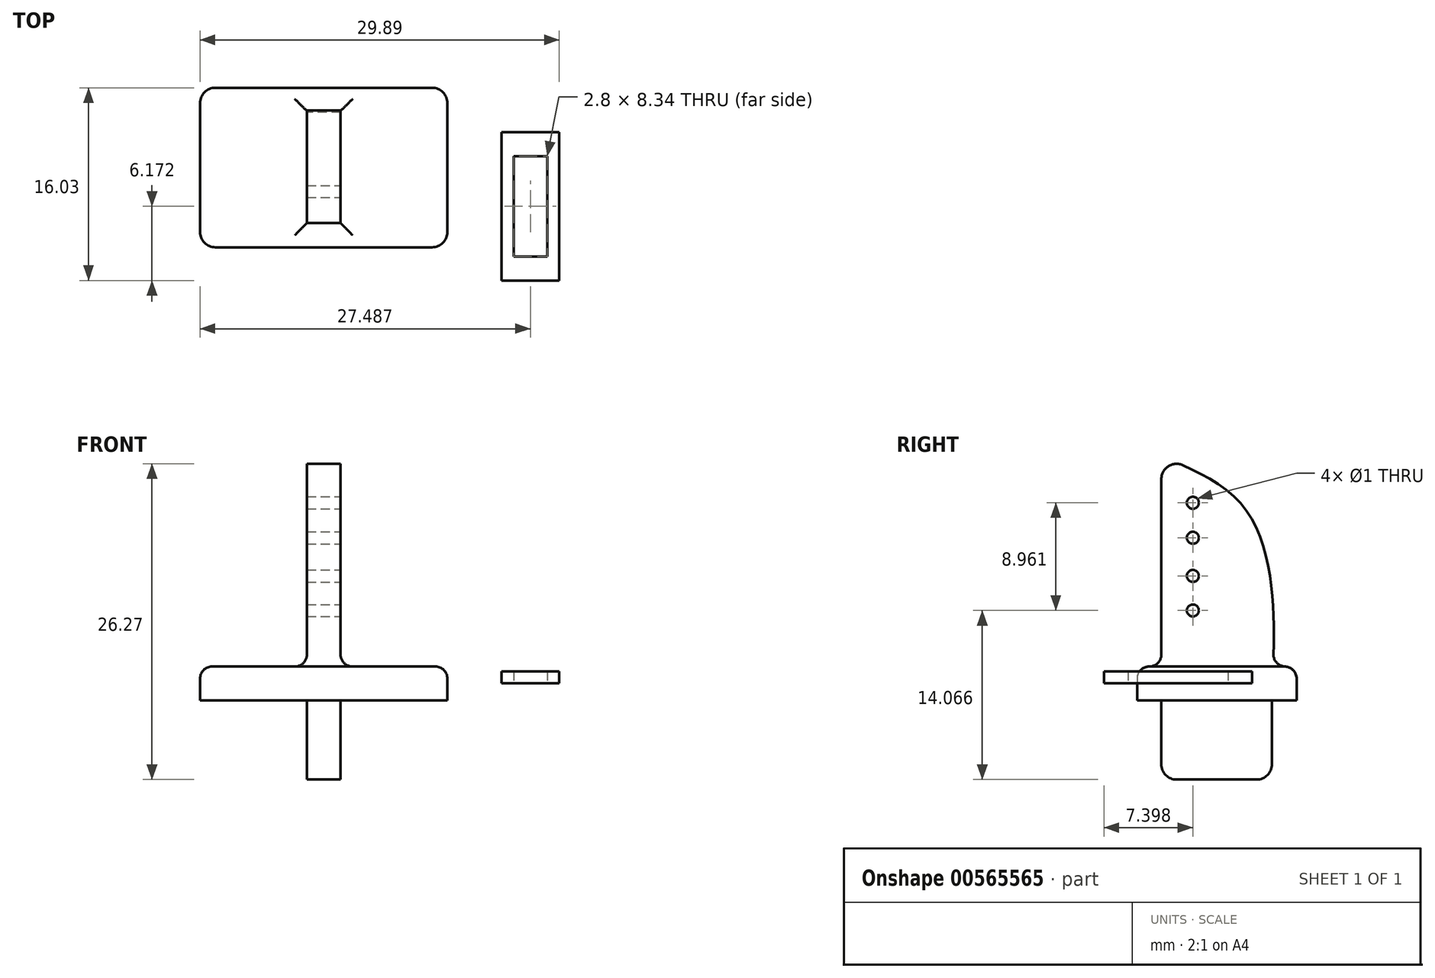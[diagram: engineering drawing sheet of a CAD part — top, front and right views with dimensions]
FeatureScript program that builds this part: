
annotation { "Feature Type Name" : "Feature", "Feature Type Description" : "" }
export const myFeature = defineFeature(function(context is Context, id is Id, definition is map)
    precondition{}
    {
        {
            var Q0;
            Q0=qCreatedBy(makeId("Top.planeOp"),FACE);
            var sketch = newSketch(context, id + "F0", { "sketchPlane" : qUnion([Q0])});
            skLineSegment(sketch, "E0.bottom", {"start": v(10.29, -6.63) * mm, "end": v(-10.29, -6.63) * mm});
            skLineSegment(sketch, "E0.top", {"start": v(10.29, 6.63) * mm, "end": v(-10.29, 6.63) * mm});
            skLineSegment(sketch, "E0.left", {"start": v(10.29, -6.63) * mm, "end": v(10.29, 6.63) * mm});
            skLineSegment(sketch, "E0.right", {"start": v(-10.29, -6.63) * mm, "end": v(-10.29, 6.63) * mm});
            skPoint(sketch, "E0.middle", {"position": v(0, 0) * mm});
            skLineSegment(sketch, "E1", {"start": v(0, 6.63) * mm, "end": v(0, -6.63) * mm});
            skPoint(sketch, "E2", {"position": v(0, 4.47) * mm});
            skPoint(sketch, "E3", {"position": v(0, -3.66) * mm});
            skSolve(sketch);
        }
        {
            var Q0;
            Q0=qCreatedBy(makeId("Right.planeOp"),FACE);
            var sketch = newSketch(context, id + "F1", { "sketchPlane" : qUnion([Q0])});
            skLineSegment(sketch, "E4", {"start": v(-4.62, 0) * mm, "end": v(-4.62, 19) * mm});
            skLineSegment(sketch, "E5", {"start": v(-4.62, 0) * mm, "end": v(-4.62, -8) * mm});
            skLineSegment(sketch, "E6", {"start": v(-4.62, -8) * mm, "end": v(4.58, -8) * mm});
            skLineSegment(sketch, "E7", {"start": v(4.58, 0) * mm, "end": v(4.58, -8) * mm});
            skFitSpline(sketch, "E8", {"points": [v(4.58, 0) * mm, v(4.58, 7.59) * mm, v(1.93, 15.03) * mm, v(-4.62, 19) * mm], "startDerivative": vector(1.47, 21.84) * mm, "endDerivative": vector(-18.58, 9.08) * mm});
            skPoint(sketch, "E9", {"position": v(-2, 15.03) * mm});
            skPoint(sketch, "E10", {"position": v(-2, 12.12) * mm});
            skPoint(sketch, "E11", {"position": v(-2, 8.94) * mm});
            skPoint(sketch, "E12", {"position": v(-2, 6.07) * mm});
            skLineSegment(sketch, "E13", {"start": v(-2, -5.7) * mm, "end": v(-2, 21.25) * mm, "construction": true});
            skSolve(sketch);
        }
        {
            var Q0;
            Q0=makeQuery(id+"F1.imprint","IMPRINT",FACE,{"disambiguationData":[TD([[makeQuery(id+"F1.imprint","IMPRINT",EDGE,{"derivedFrom":sQuery(id+"F1.wireOp",EDGE,"E4")}),-1.0]])]});
            extrude(context, id + "F2", {"entities" : qUnion([Q0]), "endBound" : BoundingType.SYMMETRIC, "depth" : 2.8 * mm, "offsetDistance" : 25.4 * mm});
        }
        {
            var Q0;
            {var subQ0=sQuery(id+"F0.wireOp",EDGE,"E0.left");Q0=makeQuery(id+"F0.imprint","IMPRINT",FACE,{"disambiguationData":[TD([[makeQuery(id+"F0.imprint","IMPRINT",EDGE,{"derivedFrom":subQ0}),1.0]])]});}
            var Q1;
            {var subQ0=sQuery(id+"F0.wireOp",EDGE,"E0.right");Q1=makeQuery(id+"F0.imprint","IMPRINT",FACE,{"disambiguationData":[TD([[makeQuery(id+"F0.imprint","IMPRINT",EDGE,{"derivedFrom":subQ0}),-1.0]])]});}
            extrude(context, id + "F3", {"entities" : qUnion([Q0, Q1]), "operationType" : NewBodyOperationType.ADD, "endBound" : BoundingType.SYMMETRIC, "depth" : 2.8 * mm, "offsetDistance" : 25.4 * mm});
        }
        {
            var Q0;
            Q0=makeQuery(id+"F2.opExtrude","SWEPT_EDGE",EDGE,{"disambiguationData":[OSD([sQuery(id+"F1.wireOp",EDGE,"E5"),sQuery(id+"F1.wireOp",EDGE,"E6")])]});
            var Q1;
            Q1=makeQuery(id+"F2.opExtrude","SWEPT_EDGE",EDGE,{"disambiguationData":[OSD([sQuery(id+"F1.wireOp",EDGE,"E6"),sQuery(id+"F1.wireOp",EDGE,"E7")])]});
            var Q2;
            Q2=makeQuery(id+"F2.opExtrude","SWEPT_EDGE",EDGE,{"disambiguationData":[OSD([sQuery(id+"F1.wireOp",EDGE,"E4"),sQuery(id+"F1.wireOp",EDGE,"E8")])]});
            fillet(context, id + "F4", {"entities" : qUnion([Q0, Q1, Q2]), "radius" : 1.27 * mm, "tangentPropagation" : true, "allowEdgeOverflow" : false});
        }
        {
            var Q0;
            Q0=makeQuery(id+"F3.opExtrude","SWEPT_EDGE",EDGE,{"disambiguationData":[OSD([sQuery(id+"F0.wireOp",EDGE,"E0.bottom"),sQuery(id+"F0.wireOp",EDGE,"E0.left")])]});
            var Q1;
            Q1=makeQuery(id+"F3.opExtrude","SWEPT_EDGE",EDGE,{"disambiguationData":[OSD([sQuery(id+"F0.wireOp",EDGE,"E0.bottom"),sQuery(id+"F0.wireOp",EDGE,"E0.right")])]});
            var Q2;
            Q2=makeQuery(id+"F3.opExtrude","SWEPT_EDGE",EDGE,{"disambiguationData":[OSD([sQuery(id+"F0.wireOp",EDGE,"E0.top"),sQuery(id+"F0.wireOp",EDGE,"E0.right")])]});
            var Q3;
            Q3=makeQuery(id+"F3.opExtrude","SWEPT_EDGE",EDGE,{"disambiguationData":[OSD([sQuery(id+"F0.wireOp",EDGE,"E0.top"),sQuery(id+"F0.wireOp",EDGE,"E0.left")])]});
            fillet(context, id + "F5", {"entities" : qUnion([Q0, Q1, Q2, Q3]), "radius" : 1.27 * mm, "tangentPropagation" : true, "allowEdgeOverflow" : false});
        }
        {
            var Q0;
            Q0=makeQuery(id+"F3.opExtrude","CAP_EDGE",EDGE,{"disambiguationData":[OSD([sQuery(id+"F0.wireOp",EDGE,"E0.top")])],"isStart":false});
            fillet(context, id + "F6", {"entities" : qUnion([Q0]), "radius" : 1 * mm, "tangentPropagation" : true, "allowEdgeOverflow" : false});
        }
        {
            var Q0;
            Q0=makeQuery(id+"F3.boolean.opBoolean","INTERSECT",EDGE,{"derivedFrom":[makeQuery(id+"F2.opExtrude","CAP_FACE",FACE,{"disambiguationData":[OSD([sQuery(id+"F1.wireOp",EDGE,"E4"),sQuery(id+"F1.wireOp",EDGE,"E5"),sQuery(id+"F1.wireOp",EDGE,"E6"),sQuery(id+"F1.wireOp",EDGE,"E7"),sQuery(id+"F1.wireOp",EDGE,"E8")])],"isStart":false}),makeQuery(id+"F3.opExtrude","CAP_FACE",FACE,{"disambiguationData":[OSD([sQuery(id+"F0.wireOp",EDGE,"E0.bottom"),sQuery(id+"F0.wireOp",EDGE,"E0.top"),sQuery(id+"F0.wireOp",EDGE,"E0.left"),sQuery(id+"F0.wireOp",EDGE,"E0.right")])],"isStart":false})]});
            var Q1;
            Q1=makeQuery(id+"F3.boolean.opBoolean","INTERSECT",EDGE,{"derivedFrom":[makeQuery(id+"F2.opExtrude","SWEPT_FACE",FACE,{"disambiguationData":[OSD([sQuery(id+"F1.wireOp",EDGE,"E4"),sQuery(id+"F1.wireOp",EDGE,"E5")])]}),makeQuery(id+"F3.opExtrude","CAP_FACE",FACE,{"disambiguationData":[OSD([sQuery(id+"F0.wireOp",EDGE,"E0.bottom"),sQuery(id+"F0.wireOp",EDGE,"E0.top"),sQuery(id+"F0.wireOp",EDGE,"E0.left"),sQuery(id+"F0.wireOp",EDGE,"E0.right")])],"isStart":false})]});
            var Q2;
            Q2=makeQuery(id+"F3.boolean.opBoolean","INTERSECT",EDGE,{"derivedFrom":[makeQuery(id+"F2.opExtrude","CAP_FACE",FACE,{"disambiguationData":[OSD([sQuery(id+"F1.wireOp",EDGE,"E4"),sQuery(id+"F1.wireOp",EDGE,"E5"),sQuery(id+"F1.wireOp",EDGE,"E6"),sQuery(id+"F1.wireOp",EDGE,"E7"),sQuery(id+"F1.wireOp",EDGE,"E8")])],"isStart":true}),makeQuery(id+"F3.opExtrude","CAP_FACE",FACE,{"disambiguationData":[OSD([sQuery(id+"F0.wireOp",EDGE,"E0.bottom"),sQuery(id+"F0.wireOp",EDGE,"E0.top"),sQuery(id+"F0.wireOp",EDGE,"E0.left"),sQuery(id+"F0.wireOp",EDGE,"E0.right")])],"isStart":false})]});
            var Q3;
            Q3=makeQuery(id+"F3.boolean.opBoolean","INTERSECT",EDGE,{"derivedFrom":[makeQuery(id+"F2.opExtrude","SWEPT_FACE",FACE,{"disambiguationData":[OSD([sQuery(id+"F1.wireOp",EDGE,"E8")])]}),makeQuery(id+"F3.opExtrude","CAP_FACE",FACE,{"disambiguationData":[OSD([sQuery(id+"F0.wireOp",EDGE,"E0.bottom"),sQuery(id+"F0.wireOp",EDGE,"E0.top"),sQuery(id+"F0.wireOp",EDGE,"E0.left"),sQuery(id+"F0.wireOp",EDGE,"E0.right")])],"isStart":false})]});
            fillet(context, id + "F7", {"entities" : qUnion([Q0, Q1, Q2, Q3]), "radius" : 1 * mm, "tangentPropagation" : true, "allowEdgeOverflow" : false});
        }
        {
            var Q0;
            Q0=sQuery(id+"F1.wireOp",VERTEX,"E9");
            var Q1;
            Q1=sQuery(id+"F1.wireOp",VERTEX,"E10");
            var Q2;
            Q2=sQuery(id+"F1.wireOp",VERTEX,"E11");
            var Q3;
            Q3=sQuery(id+"F1.wireOp",VERTEX,"E12");
            var Q4;
            Q4=makeQuery(id+"F2.opExtrude","SWEPT_BODY",BODY,{"disambiguationData":[OSD([sQuery(id+"F1.wireOp",EDGE,"E4"),sQuery(id+"F1.wireOp",EDGE,"E5"),sQuery(id+"F1.wireOp",EDGE,"E6"),sQuery(id+"F1.wireOp",EDGE,"E7"),sQuery(id+"F1.wireOp",EDGE,"E8")])]});
            hole(context, id + "F8", {"style" : HoleStyle.SIMPLE, "endStyle" : HoleEndStyle.THROUGH, "holeDiameter" : 1 * mm, "majorDiameter" : 5 * mm, "isTappedThrough" : true, "tappedDepth" : 12.7 * mm, "tapClearance" : 3, "startFromSketch" : true, "locations" : qUnion([Q0, Q1, Q2, Q3]), "scope" : qUnion([Q4])});
        }
        {
            var Q0;
            Q0=sQuery(id+"F1.wireOp",VERTEX,"E9");
            var Q1;
            Q1=sQuery(id+"F1.wireOp",VERTEX,"E10");
            var Q2;
            Q2=sQuery(id+"F1.wireOp",VERTEX,"E11");
            var Q3;
            Q3=sQuery(id+"F1.wireOp",VERTEX,"E12");
            var Q4;
            Q4=makeQuery(id+"F2.opExtrude","SWEPT_BODY",BODY,{"disambiguationData":[OSD([sQuery(id+"F1.wireOp",EDGE,"E4"),sQuery(id+"F1.wireOp",EDGE,"E5"),sQuery(id+"F1.wireOp",EDGE,"E6"),sQuery(id+"F1.wireOp",EDGE,"E7"),sQuery(id+"F1.wireOp",EDGE,"E8")])]});
            hole(context, id + "F9", {"style" : HoleStyle.SIMPLE, "endStyle" : HoleEndStyle.THROUGH, "oppositeDirection" : true, "holeDiameter" : 1 * mm, "majorDiameter" : 5 * mm, "isTappedThrough" : true, "tappedDepth" : 12.7 * mm, "tapClearance" : 3, "startFromSketch" : true, "locations" : qUnion([Q0, Q1, Q2, Q3]), "scope" : qUnion([Q4])});
        }
        {
            var Q0;
            Q0=qCreatedBy(makeId("Top.planeOp"),FACE);
            var sketch = newSketch(context, id + "F10", { "sketchPlane" : qUnion([Q0])});
            skLineSegment(sketch, "E14.bottom", {"start": v(18.6, -7.4) * mm, "end": v(15.8, -7.4) * mm});
            skLineSegment(sketch, "E14.top", {"start": v(18.6, 0.94) * mm, "end": v(15.8, 0.94) * mm});
            skLineSegment(sketch, "E14.left", {"start": v(18.6, -7.4) * mm, "end": v(18.6, 0.94) * mm});
            skLineSegment(sketch, "E14.right", {"start": v(15.8, -7.4) * mm, "end": v(15.8, 0.94) * mm});
            skLineSegment(sketch, "E15.bottom", {"start": v(19.6, -9.4) * mm, "end": v(14.8, -9.4) * mm});
            skLineSegment(sketch, "E15.top", {"start": v(19.6, 2.94) * mm, "end": v(14.8, 2.94) * mm});
            skLineSegment(sketch, "E15.left", {"start": v(19.6, -9.4) * mm, "end": v(19.6, 2.94) * mm});
            skLineSegment(sketch, "E15.right", {"start": v(14.8, -9.4) * mm, "end": v(14.8, 2.94) * mm});
            skSolve(sketch);
        }
        {
            var Q0;
            Q0=makeQuery(id+"F10.imprint","IMPRINT",FACE,{"disambiguationData":[TD([[makeQuery(id+"F10.imprint","IMPRINT",EDGE,{"derivedFrom":sQuery(id+"F10.wireOp",EDGE,"E14.bottom")}),1.0]])]});
            extrude(context, id + "F11", {"entities" : qUnion([Q0]), "depth" : 1 * mm, "offsetDistance" : 25 * mm});
        }
    });
